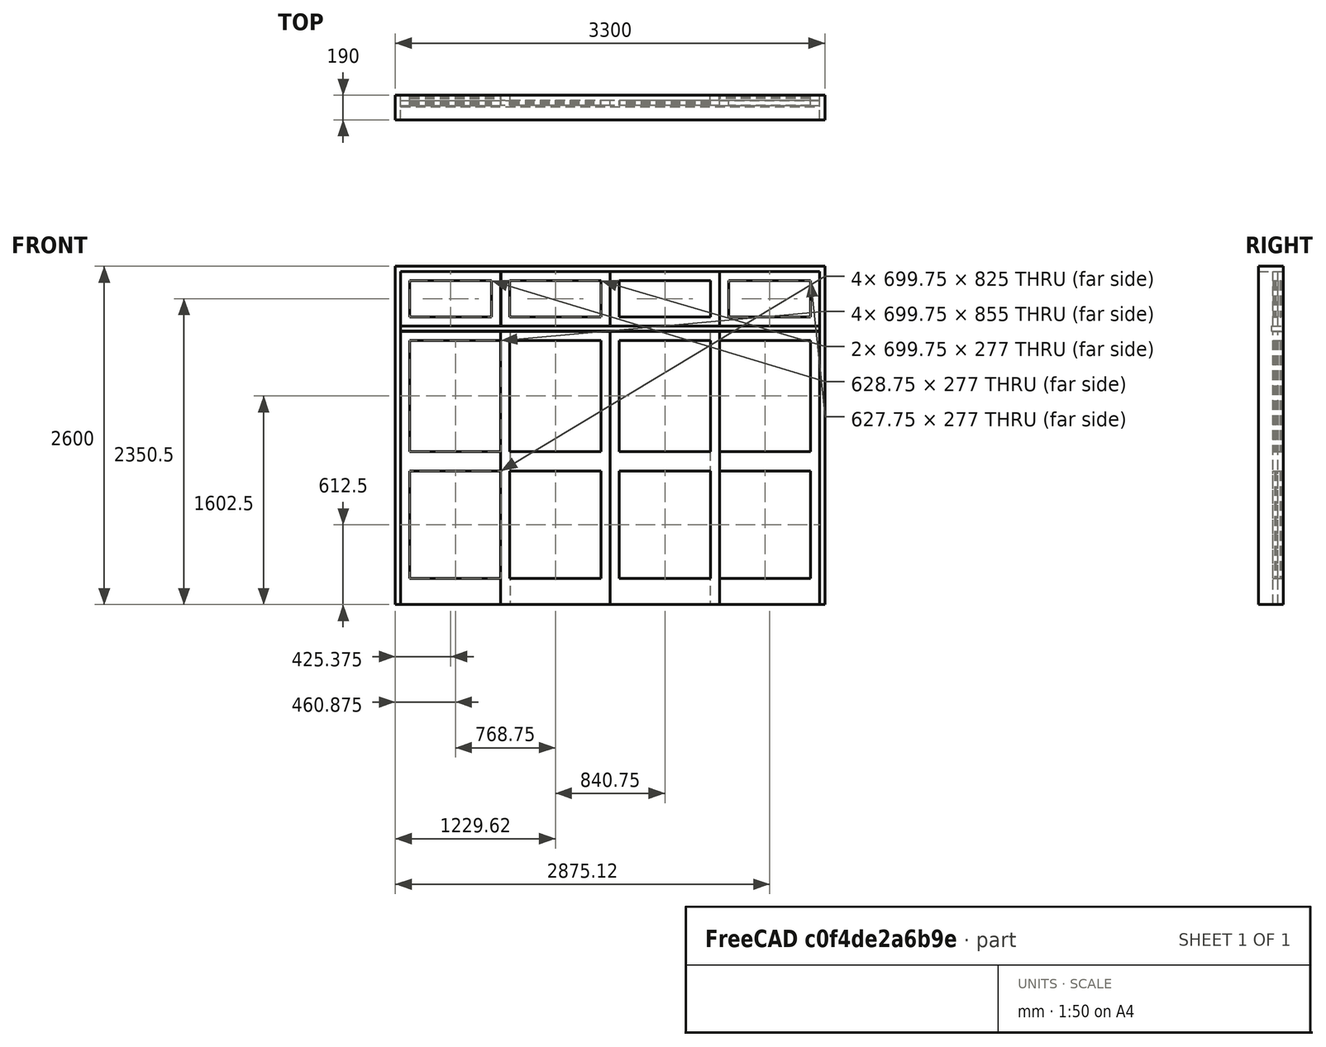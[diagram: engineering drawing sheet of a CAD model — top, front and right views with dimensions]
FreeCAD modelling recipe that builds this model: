
FCSTD DOCUMENT  (FreeCAD 0.16R6704 (Git))
Label: Slinding door 4 sheets with glass and transom
License: CreativeCommons Attribution
LicenseURL: http://creativecommons.org/licenses/by/4.0/
objects: Sketcher::SketchObject×1, Part::FeaturePython×1
note: 2 computed .brp shape members not serialized (recipe doc carries the construction recipe); baked Part::Feature solids carry a one-line shape summary decoded from their .brp

FEATURE [Sketcher::SketchObject] Sketch181  label="Sketch"
  Placement = pos=(0,0,0) rot=(1,0,0;1.5708rad)
  sketch-geometry (96):
    g0: LineSegment StartX=0 StartY=0 StartZ=0 EndX=3300 EndY=0 EndZ=0
    g1: LineSegment StartX=3300 StartY=0 StartZ=0 EndX=3300 EndY=2600 EndZ=0
    g2: LineSegment StartX=3300 StartY=2600 StartZ=0 EndX=0 EndY=2600 EndZ=0
    g3: LineSegment StartX=0 StartY=2600 StartZ=0 EndX=0 EndY=0 EndZ=0
    g4: LineSegment StartX=40 StartY=0 StartZ=0 EndX=3260 EndY=0 EndZ=0
    g5: LineSegment StartX=3260 StartY=0 StartZ=0 EndX=3260 EndY=2560 EndZ=0
    g6: LineSegment StartX=3260 StartY=2560 StartZ=0 EndX=40 EndY=2560 EndZ=0
    g7: LineSegment StartX=40 StartY=2560 StartZ=0 EndX=40 EndY=0 EndZ=0
    g8: LineSegment StartX=111 StartY=2030 StartZ=0 EndX=810.75 EndY=2030 EndZ=0
    g9: LineSegment StartX=810.75 StartY=2030 StartZ=0 EndX=810.75 EndY=1175 EndZ=0
    g10: LineSegment StartX=810.75 StartY=1175 StartZ=0 EndX=111 EndY=1175 EndZ=0
    g11: LineSegment StartX=111 StartY=1175 StartZ=0 EndX=111 EndY=2030 EndZ=0
    g12: LineSegment StartX=111 StartY=1025 StartZ=0 EndX=810.75 EndY=1025 EndZ=0
    g13: LineSegment StartX=810.75 StartY=1025 StartZ=0 EndX=810.75 EndY=200 EndZ=0
    g14: LineSegment StartX=810.75 StartY=200 StartZ=0 EndX=111 EndY=200 EndZ=0
    g15: LineSegment StartX=111 StartY=200 StartZ=0 EndX=111 EndY=1025 EndZ=0
    g16: LineSegment [constr] StartX=-278 StartY=1100 StartZ=0 EndX=2205 EndY=1100 EndZ=0
    g17: LineSegment StartX=41 StartY=2100 StartZ=0 EndX=880.75 EndY=2100 EndZ=0
    g18: LineSegment StartX=880.75 StartY=2100 StartZ=0 EndX=880.75 EndY=1 EndZ=0
    g19: LineSegment StartX=880.75 StartY=1 StartZ=0 EndX=41 EndY=1 EndZ=0
    g20: LineSegment StartX=41 StartY=1 StartZ=0 EndX=41 EndY=2100 EndZ=0
    g21: LineSegment [constr] StartX=845.25 StartY=2946 StartZ=0 EndX=845.25 EndY=-202.596 EndZ=0
    g22: LineSegment StartX=1579.5 StartY=2030 StartZ=0 EndX=879.75 EndY=2030 EndZ=0
    g23: LineSegment StartX=879.75 StartY=2030 StartZ=0 EndX=879.75 EndY=1175 EndZ=0
    g24: LineSegment StartX=879.75 StartY=1175 StartZ=0 EndX=1579.5 EndY=1175 EndZ=0
    g25: LineSegment StartX=1579.5 StartY=1175 StartZ=0 EndX=1579.5 EndY=2030 EndZ=0
    g26: LineSegment StartX=1579.5 StartY=1025 StartZ=0 EndX=879.75 EndY=1025 EndZ=0
    g27: LineSegment StartX=879.75 StartY=1025 StartZ=0 EndX=879.75 EndY=200 EndZ=0
    g28: LineSegment StartX=879.75 StartY=200 StartZ=0 EndX=1579.5 EndY=200 EndZ=0
    g29: LineSegment StartX=1579.5 StartY=200 StartZ=0 EndX=1579.5 EndY=1025 EndZ=0
    g30: LineSegment StartX=1649.5 StartY=2100 StartZ=0 EndX=809.75 EndY=2100 EndZ=0
    g31: LineSegment StartX=809.75 StartY=2100 StartZ=0 EndX=809.75 EndY=1 EndZ=0
    g32: LineSegment StartX=809.75 StartY=1 StartZ=0 EndX=1649.5 EndY=1 EndZ=0
    g33: LineSegment StartX=1649.5 StartY=1 StartZ=0 EndX=1649.5 EndY=2100 EndZ=0
    g34: LineSegment StartX=41 StartY=2559 StartZ=0 EndX=809.75 EndY=2559 EndZ=0
    g35: LineSegment StartX=809.75 StartY=2559 StartZ=0 EndX=809.75 EndY=2142 EndZ=0
    g36: LineSegment StartX=809.75 StartY=2142 StartZ=0 EndX=41 EndY=2142 EndZ=0
    g37: LineSegment StartX=41 StartY=2142 StartZ=0 EndX=41 EndY=2559 EndZ=0
    g38: LineSegment StartX=111 StartY=2489 StartZ=0 EndX=739.75 EndY=2489 EndZ=0
    g39: LineSegment StartX=739.75 StartY=2489 StartZ=0 EndX=739.75 EndY=2212 EndZ=0
    g40: LineSegment StartX=739.75 StartY=2212 StartZ=0 EndX=111 EndY=2212 EndZ=0
    g41: LineSegment StartX=111 StartY=2212 StartZ=0 EndX=111 EndY=2489 EndZ=0
    g42: LineSegment StartX=879.75 StartY=2489 StartZ=0 EndX=1579.5 EndY=2489 EndZ=0
    g43: LineSegment StartX=1579.5 StartY=2489 StartZ=0 EndX=1579.5 EndY=2212 EndZ=0
    g44: LineSegment StartX=1579.5 StartY=2212 StartZ=0 EndX=879.75 EndY=2212 EndZ=0
    g45: LineSegment StartX=879.75 StartY=2212 StartZ=0 EndX=879.75 EndY=2489 EndZ=0
    g46: LineSegment StartX=41 StartY=2141 StartZ=0 EndX=3259 EndY=2141 EndZ=0
    g47: LineSegment StartX=3259 StartY=2141 StartZ=0 EndX=3259 EndY=2101 EndZ=0
    g48: LineSegment StartX=3259 StartY=2101 StartZ=0 EndX=41 EndY=2101 EndZ=0
    g49: LineSegment StartX=41 StartY=2101 StartZ=0 EndX=41 EndY=2141 EndZ=0
    g50: LineSegment [constr] StartX=1650 StartY=3215.43 StartZ=0 EndX=1650 EndY=-368.353 EndZ=0
    g51: LineSegment StartX=3189 StartY=2030 StartZ=0 EndX=2489.25 EndY=2030 EndZ=0
    g52: LineSegment StartX=2489.25 StartY=2030 StartZ=0 EndX=2489.25 EndY=1175 EndZ=0
    g53: LineSegment StartX=2489.25 StartY=1175 StartZ=0 EndX=3189 EndY=1175 EndZ=0
    g54: LineSegment StartX=3189 StartY=1175 StartZ=0 EndX=3189 EndY=2030 EndZ=0
    g55: LineSegment StartX=3189 StartY=1025 StartZ=0 EndX=2489.25 EndY=1025 EndZ=0
    g56: LineSegment StartX=2489.25 StartY=1025 StartZ=0 EndX=2489.25 EndY=200 EndZ=0
    g57: LineSegment StartX=2489.25 StartY=200 StartZ=0 EndX=3189 EndY=200 EndZ=0
    g58: LineSegment StartX=3189 StartY=200 StartZ=0 EndX=3189 EndY=1025 EndZ=0
    g59: LineSegment StartX=3259 StartY=2100 StartZ=0 EndX=2419.25 EndY=2100 EndZ=0
    g60: LineSegment StartX=2419.25 StartY=2100 StartZ=0 EndX=2419.25 EndY=1 EndZ=0
    g61: LineSegment StartX=2419.25 StartY=1 StartZ=0 EndX=3259 EndY=1 EndZ=0
    g62: LineSegment StartX=3259 StartY=1 StartZ=0 EndX=3259 EndY=2100 EndZ=0
    g63: LineSegment [constr] StartX=2454.75 StartY=2946 StartZ=0 EndX=2454.75 EndY=-202.598 EndZ=0
    g64: LineSegment StartX=1720.5 StartY=2030 StartZ=0 EndX=2420.25 EndY=2030 EndZ=0
    g65: LineSegment StartX=2420.25 StartY=2030 StartZ=0 EndX=2420.25 EndY=1175 EndZ=0
    g66: LineSegment StartX=2420.25 StartY=1175 StartZ=0 EndX=1720.5 EndY=1175 EndZ=0
    g67: LineSegment StartX=1720.5 StartY=1175 StartZ=0 EndX=1720.5 EndY=2030 EndZ=0
    g68: LineSegment StartX=1720.5 StartY=1025 StartZ=0 EndX=2420.25 EndY=1025 EndZ=0
    g69: LineSegment StartX=2420.25 StartY=1025 StartZ=0 EndX=2420.25 EndY=200 EndZ=0
    g70: LineSegment StartX=2420.25 StartY=200 StartZ=0 EndX=1720.5 EndY=200 EndZ=0
    g71: LineSegment StartX=1720.5 StartY=200 StartZ=0 EndX=1720.5 EndY=1025 EndZ=0
    g72: LineSegment StartX=1650.5 StartY=2100 StartZ=0 EndX=2490.25 EndY=2100 EndZ=0
    g73: LineSegment StartX=2490.25 StartY=2100 StartZ=0 EndX=2490.25 EndY=1 EndZ=0
    g74: LineSegment StartX=2490.25 StartY=1 StartZ=0 EndX=1650.5 EndY=1 EndZ=0
    g75: LineSegment StartX=1650.5 StartY=1 StartZ=0 EndX=1650.5 EndY=2100 EndZ=0
    g76: LineSegment StartX=2490.25 StartY=2559 StartZ=0 EndX=1650.5 EndY=2559 EndZ=0
    g77: LineSegment StartX=1650.5 StartY=2559 StartZ=0 EndX=1650.5 EndY=2142 EndZ=0
    g78: LineSegment StartX=1650.5 StartY=2142 StartZ=0 EndX=2490.25 EndY=2142 EndZ=0
    g79: LineSegment StartX=2490.25 StartY=2142 StartZ=0 EndX=2490.25 EndY=2559 EndZ=0
    g80: LineSegment StartX=3189 StartY=2489 StartZ=0 EndX=2561.25 EndY=2489 EndZ=0
    g81: LineSegment StartX=2561.25 StartY=2489 StartZ=0 EndX=2561.25 EndY=2212 EndZ=0
    g82: LineSegment StartX=2561.25 StartY=2212 StartZ=0 EndX=3189 EndY=2212 EndZ=0
    g83: LineSegment StartX=3189 StartY=2212 StartZ=0 EndX=3189 EndY=2489 EndZ=0
    g84: LineSegment StartX=2420.25 StartY=2489 StartZ=0 EndX=1720.5 EndY=2489 EndZ=0
    g85: LineSegment StartX=1720.5 StartY=2489 StartZ=0 EndX=1720.5 EndY=2212 EndZ=0
    g86: LineSegment StartX=1720.5 StartY=2212 StartZ=0 EndX=2420.25 EndY=2212 EndZ=0
    g87: LineSegment StartX=2420.25 StartY=2212 StartZ=0 EndX=2420.25 EndY=2489 EndZ=0
    g88: LineSegment StartX=2491.25 StartY=2559 StartZ=0 EndX=3259 EndY=2559 EndZ=0
    g89: LineSegment StartX=3259 StartY=2559 StartZ=0 EndX=3259 EndY=2142 EndZ=0
    g90: LineSegment StartX=3259 StartY=2142 StartZ=0 EndX=2491.25 EndY=2142 EndZ=0
    g91: LineSegment StartX=2491.25 StartY=2142 StartZ=0 EndX=2491.25 EndY=2559 EndZ=0
    g92: LineSegment StartX=1649.5 StartY=2559 StartZ=0 EndX=810.75 EndY=2559 EndZ=0
    g93: LineSegment StartX=810.75 StartY=2559 StartZ=0 EndX=810.75 EndY=2142 EndZ=0
    g94: LineSegment StartX=810.75 StartY=2142 StartZ=0 EndX=1649.5 EndY=2142 EndZ=0
    g95: LineSegment StartX=1649.5 StartY=2142 StartZ=0 EndX=1649.5 EndY=2559 EndZ=0
  constraints (283):
    c: Coincident(g0,g1)
    c: Coincident(g1,g2)
    c: Coincident(g2,g3)
    c: Coincident(g3,g0)
    c: Horizontal(g0)
    c: Horizontal(g2)
    c: Vertical(g1)
    c: Vertical(g3)
    c: Coincident(g4,g5)
    c: Coincident(g5,g6)
    c: Coincident(g6,g7)
    c: Coincident(g7,g4)
    c: Horizontal(g4)
    c: Horizontal(g6)
    c: Vertical(g5)
    c: Vertical(g7)
    c: DistanceY(g1) = 2600  'Altura do vão'
    c: DistanceX(g0) = 3300  'Largura do vão'
    c: DistanceY(g6,g2) = 40  'Altura batente superior'
    c: DistanceX(g2,g6) = 40  'Largura do batente 1'
    c: DistanceX(g4,g0) = 40  'Largura do batente 2'
    c: DistanceY(g0,g4) = 0
    c: Coincident(g0,g-1)
    c: Coincident(g8,g9)
    c: Coincident(g9,g10)
    c: Coincident(g10,g11)
    c: Coincident(g11,g8)
    c: Horizontal(g8)
    c: Horizontal(g10)
    c: Vertical(g9)
    c: Vertical(g11)
    c: Coincident(g12,g13)
    c: Coincident(g13,g14)
    c: Coincident(g14,g15)
    c: Coincident(g15,g12)
    c: Horizontal(g12)
    c: Horizontal(g14)
    c: Vertical(g13)
    c: Vertical(g15)
    c: DistanceX(g10,g12) = 0
    c: DistanceX(g9,g12) = 0
    c: DistanceY(g12,g10) = 150  'Altura do montante intermediário porta'
    c: DistanceY(g-1,g14) = 200  'Altura moldura inferior porta'
    c: Horizontal(g16)
    c: Symmetric(g10,g12,g16)
    c: DistanceY(g-1,g16) = 1100  'Altura da divisão intermediária porta'
    c: Coincident(g17,g18)
    c: Coincident(g18,g19)
    c: Coincident(g19,g20)
    c: Horizontal(g17)
    c: Horizontal(g19)
    c: Vertical(g18)
    c: Vertical(g20)
    c: DistanceY(g4,g18) = 1
    c: Vertical(g21)  'Constraint59'
    c: Coincident(g22,g23)  'Constraint57'
    c: Coincident(g23,g24)
    c: Coincident(g24,g25)
    c: Coincident(g25,g22)
    c: Horizontal(g22)
    c: Horizontal(g24)
    c: Vertical(g23)
    c: Vertical(g25)
    c: Coincident(g26,g27)
    c: Coincident(g27,g28)
    c: Coincident(g28,g29)
    c: Coincident(g29,g26)
    c: Horizontal(g26)
    c: Horizontal(g28)
    c: Vertical(g27)
    c: Vertical(g29)
    c: Coincident(g30,g31)
    c: Coincident(g31,g32)
    c: Coincident(g32,g33)
    c: Horizontal(g30)
    c: Horizontal(g32)
    c: Vertical(g31)
    c: Vertical(g33)
    c: DistanceY(g8,g22) = 0
    c: DistanceY(g9,g23) = 0
    c: DistanceY(g26,g12) = 0
    c: DistanceY(g18,g31) = 0
    c: Symmetric(g8,g22,g21)
    c: DistanceX(g24,g26) = 0
    c: Coincident(g30,g33)
    c: DistanceY(g8,g17) = 70  'Altura moldura porta'
    c: Coincident(g34,g35)  'Constraint94'
    c: Coincident(g35,g36)  'Constraint93'
    c: Coincident(g36,g37)  'Constraint92'
    c: Coincident(g37,g34)  'Constraint90'
    c: Horizontal(g34)
    c: Horizontal(g36)
    c: Vertical(g35)
    c: Vertical(g37)
    c: Coincident(g38,g39)
    c: Coincident(g39,g40)
    c: Coincident(g40,g41)
    c: Coincident(g41,g38)
    c: Horizontal(g38)
    c: Horizontal(g40)
    c: Vertical(g39)
    c: Vertical(g41)
    c: Coincident(g42,g43)
    c: Coincident(g43,g44)
    c: Coincident(g44,g45)
    c: Coincident(g45,g42)
    c: Horizontal(g42)
    c: Horizontal(g44)
    c: Vertical(g43)
    c: Vertical(g45)
    c: Coincident(g46,g47)
    c: Coincident(g47,g48)
    c: Coincident(g48,g49)
    c: Coincident(g49,g46)
    c: Horizontal(g46)
    c: Horizontal(g48)
    c: Vertical(g47)
    c: Vertical(g49)
    c: DistanceX(g17,g48) = 0
    c: DistanceY(g17,g48) = 1  'Constraint129'
    c: DistanceY(g47,g46) = 40  'Batente bandeira'
    c: DistanceY(g46,g35) = 1  'Constraint127'
    c: DistanceX(g46,g36) = 0  'Constraint124'
    c: DistanceY(g34,g6) = 1
    c: DistanceX(g40,g8) = 0
    c: DistanceY(g36,g40) = 70  'Moldura inferior bandeira'
    c: DistanceY(g39,g44) = 0  'Constraint132'
    c: DistanceX(g43,g22) = 0  'Constraint128'
    c: DistanceY(g38,g42) = 0
    c: DistanceY(g38,g34) = 70  'Altura moldura superior bandeira'
    c: DistanceY(g-1,g17) = 2100  'Altura porta'
    c: Coincident(g17,g20)
    c: DistanceY(g27,g13) = 0
    c: DistanceX(g17,g8) = 70  'Largura montante vertica porta 1'
    c: DistanceX(g30,g22) = 70  'Montante vertical 1 porta 2'
    c: DistanceX(g8,g17) = 70  'Montante vertical 2 porta 1'
    c: DistanceX(g23,g26) = 0  'Constraint137'
    c: DistanceX(g6,g34) = 1  'Constraint142'
    c: Vertical(g50)  'Constraint140'
    c: Symmetric(g2,g1,g50)
    c: Coincident(g51,g52)
    c: Coincident(g52,g53)
    c: Coincident(g53,g54)
    c: Coincident(g54,g51)
    c: Horizontal(g51)
    c: Horizontal(g53)
    c: Vertical(g52)
    c: Vertical(g54)
    c: Coincident(g55,g56)
    c: Coincident(g56,g57)
    c: Coincident(g57,g58)
    c: Coincident(g58,g55)
    c: Horizontal(g55)
    c: Horizontal(g57)
    c: Vertical(g56)
    c: Vertical(g58)
    c: Coincident(g59,g60)
    c: Coincident(g60,g61)
    c: Coincident(g61,g62)
    c: Horizontal(g59)
    c: Horizontal(g61)
    c: Vertical(g60)
    c: Vertical(g62)
    c: Vertical(g63)  'Constraint59'
    c: Coincident(g64,g65)  'Constraint57'
    c: Coincident(g65,g66)  'Constraint169'
    c: Coincident(g66,g67)
    c: Coincident(g67,g64)
    c: Horizontal(g64)
    c: Horizontal(g66)
    c: Vertical(g65)
    c: Vertical(g67)
    c: Coincident(g68,g69)
    c: Coincident(g69,g70)
    c: Coincident(g70,g71)
    c: Coincident(g71,g68)
    c: Horizontal(g68)
    c: Horizontal(g70)
    c: Vertical(g69)
    c: Vertical(g71)
    c: Coincident(g72,g73)
    c: Coincident(g73,g74)
    c: Coincident(g74,g75)
    c: Horizontal(g72)
    c: Horizontal(g74)
    c: Vertical(g73)
    c: Vertical(g75)
    c: Symmetric(g51,g64,g63)
    c: Coincident(g72,g75)
    c: Coincident(g76,g77)  'Constraint94'
    c: Coincident(g77,g78)  'Constraint93'
    c: Coincident(g78,g79)  'Constraint92'
    c: Coincident(g79,g76)  'Constraint90'
    c: Horizontal(g76)
    c: Horizontal(g78)
    c: Vertical(g77)
    c: Vertical(g79)
    c: Coincident(g80,g81)
    c: Coincident(g81,g82)
    c: Coincident(g82,g83)
    c: Coincident(g83,g80)
    c: Horizontal(g80)
    c: Horizontal(g82)
    c: Vertical(g81)
    c: Vertical(g83)
    c: Coincident(g84,g85)
    c: Coincident(g85,g86)
    c: Coincident(g86,g87)
    c: Coincident(g87,g84)
    c: Horizontal(g84)
    c: Horizontal(g86)
    c: Vertical(g85)
    c: Vertical(g87)
    c: Coincident(g59,g62)
    c: Coincident(g88,g89)
    c: Coincident(g89,g90)
    c: Coincident(g90,g91)
    c: Coincident(g91,g88)
    c: Horizontal(g88)
    c: Horizontal(g90)
    c: Vertical(g89)
    c: Vertical(g91)
    c: DistanceY(g88,g76) = 0
    c: DistanceX(g76,g88) = 1
    c: DistanceX(g88,g5) = 1
    c: DistanceY(g88,g5) = 1
    c: DistanceY(g78,g90) = 0
    c: DistanceX(g46,g89) = 0
    c: DistanceX(g47,g59) = 0
    c: DistanceY(g46,g89) = 1
    c: DistanceX(g77,g72) = 0
    c: Symmetric(g88,g76,g63)
    c: DistanceX(g85,g64) = 0
    c: DistanceX(g82,g51) = 0
    c: DistanceY(g80,g84) = 0
    c: DistanceY(g81,g86) = 0
    c: DistanceY(g65,g52) = 0
    c: DistanceY(g68,g55) = 0
    c: DistanceY(g69,g56) = 0
    c: DistanceY(g73,g60) = 0
    c: DistanceX(g65,g68) = 0
    c: DistanceY(g22,g64) = 0
    c: DistanceY(g66,g24) = 0
    c: DistanceY(g26,g68) = 0
    c: DistanceY(g28,g70) = 0
    c: DistanceY(g32,g74) = 0
    c: Coincident(g92,g93)
    c: Coincident(g93,g94)
    c: Coincident(g94,g95)
    c: Coincident(g95,g92)
    c: Horizontal(g92)
    c: Horizontal(g94)
    c: Vertical(g93)
    c: Vertical(g95)
    c: DistanceY(g92,g34) = 0
    c: DistanceX(g34,g92) = 1
    c: DistanceX(g38,g34) = 70  'Montante vertical 2 bandeira'
    c: DistanceY(g35,g93) = 0  'Constraint266'
    c: DistanceX(g30,g94) = 0  'Constraint264'
    c: DistanceX(g22,g44) = 0  'Constraint263'
    c: DistanceX(g84,g76) = 70  'Montante vertical 3 bandeira'
    c: DistanceY(g30,g17) = 0  'Constraint262'
    c: DistanceX(g35,g30) = 0
    c: DistanceX(g30,g8) = 1
    c: Symmetric(g30,g17,g21)
    c: DistanceX(g66,g68) = 0
    c: DistanceX(g53,g55) = 0
    c: DistanceY(g72,g59) = 0
    c: DistanceX(g64,g72) = 70  'Montante vertical 2 porta 3'
    c: DistanceX(g59,g51) = 70  'Montante vertical 1 porta 4'
    c: DistanceY(g72,g30) = 0
    c: DistanceX(g59,g64) = 1
    c: Symmetric(g59,g72,g63)
    c: DistanceY(g43,g85) = 0
    c: DistanceY(g42,g84) = 0
    c: DistanceX(g76,g84) = 70  'montante vertical 1 porta 2'
    c: DistanceX(g42,g92) = 70  'montante vertical 2 porta 1'
    c: Symmetric(g34,g92,g21)  'Constraint279'
    c: Symmetric(g92,g76,g50)
    c: DistanceX(g92,g76) = 1
    c: DistanceX(g52,g55) = 0
    c: DistanceX(g78,g72) = 0
    c: DistanceX(g88,g80) = 70  'Montante vertical 1 bandeira 4'
FEATURE [Part::FeaturePython] Window114  label="Slinding door 4 sheets with glass and transom "  # WARN: FeaturePython — macro-defined, semantics opaque (R4)
  Base = -> Sketch181
  Height = 2100
  HoleDepth = 0
  MoveWithHost = true
  Normal = (0,1,0)
  Preset = 6
  Role = 1
  Width = 900
  WindowParts = BATENTE | Frame | Wire0,Wire1 | 190.0 | 0.0 | PORTA 1 | Frame | Wire2,Wire3,Wire4 | 40.0 | 150.0 | PORTA 2 | Frame | Wire5,Wire6,Wire7 | 40.0 | 110.0 | BATENTE BANDEIRA | Frame | Wire11 | 90.0 | 100.0 | BANDEIRA | Frame | Wire10,Wire9,Wire8 | 40.0 | 110.0 | VIDRO 1 BANDEIRA | Glass panel | Wire9 | 10.0 | 125.0 | VIDRO 2 BANDEIRA | Glass panel | Wire10 | 10.0 | 125.0 | VIDRO SUPERIOR PORTA 1 | Glass panel | Wire2 | 10.0 | 165.0 | VIDRO SUPERIOR PORTA 2 | Glass panel | Wire5 | 10.0 | 125.0 | VIDRO INFERIOR PORTA 1 | Glass panel | Wire3 | 10.0 | 165.0 | VIDRO INFERIOR PORTA 2 | Glass panel | Wire6 | 10.0 | 125.0 | BANDEIRA 2 | Frame | Wire22,Wire10 | 40.0 | 110.0 | BANDEIRA 3 | Frame | Wire20,Wire18 | 40.0 | 110.0 | BANDEIRA 4 | Frame | Wire21,Wire19 | 40.0 | 110.0 | PORTA 3 | Frame | Wire17,Wire16,Wire15 | 40.0 | 110.0 | PORTA 4 | Frame | Wire14,Wire13,Wire12 | 40.0 | 150.0 | VIDRO 3 BANDEIRA | Glass panel | Wire20 | 10.0 | 125.0 | VIDRO 4 BANDEIRA | Glass panel | Wire19 | 10.0 | 165.0 | VIDRO SUPERIOR PORTA 3 | Glass panel | Wire15 | 10.0 | 125.0 | VIDRO SUPERIOR PORTA 4 | Glass panel | Wire12 | 10.0 | 165.0 | VIDRO INFERIOR PORTA3 | Glass panel | Wire16 | 10.0 | 125.0 | VIDRO INFERIOR PORTA 4 | Glass panel | Wire13 | 10.0 | 165.0
